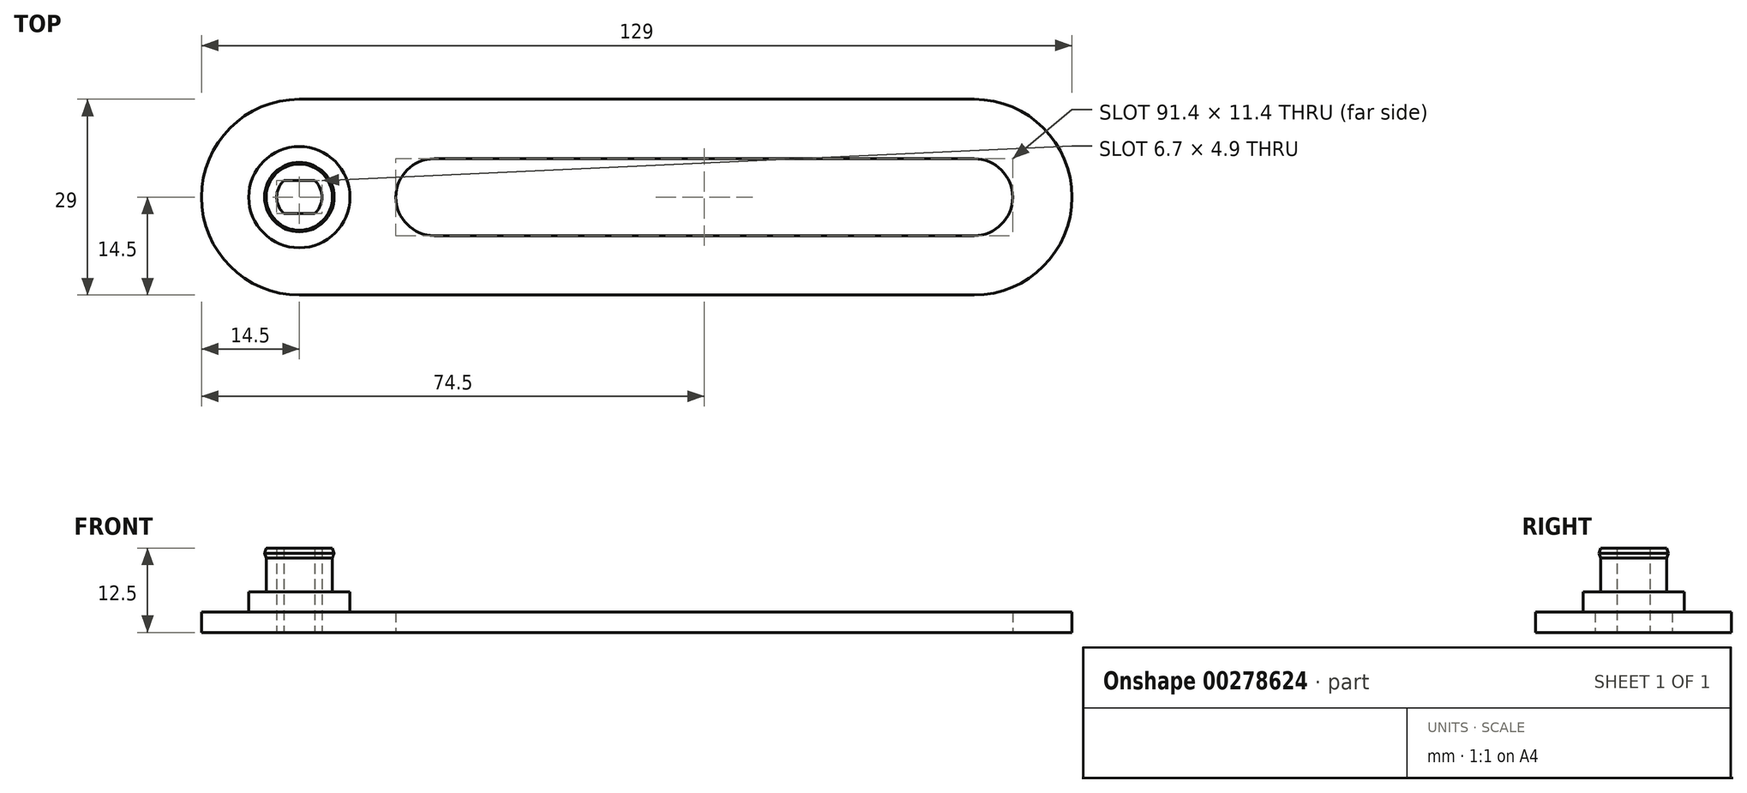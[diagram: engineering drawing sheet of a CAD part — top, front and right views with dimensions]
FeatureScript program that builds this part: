
annotation { "Feature Type Name" : "Feature", "Feature Type Description" : "" }
export const myFeature = defineFeature(function(context is Context, id is Id, definition is map)
    precondition{}
    {
        {
            assignVariable(context, id + "F0", {"name" : "e", "anyValue" : 3});
        }
        {
            assignVariable(context, id + "F1", {"name" : "h0", "anyValue" : 2});
        }
        {
            assignVariable(context, id + "F2", {"name" : "h1", "anyValue" : 3});
        }
        {
            assignVariable(context, id + "F3", {"name" : "h2", "anyValue" : 6.5});
        }
        {
            var Q0;
            Q0=qCreatedBy(makeId("Top.planeOp"),FACE);
            var sketch = newSketch(context, id + "F4", { "sketchPlane" : qUnion([Q0])});
            skCircle(sketch, "E0", {"center": v(0, 0) * mm, "radius": 5.5 * mm});
            skLineSegment(sketch, "E1.bottom", {"start": v(0, 14.5) * mm, "end": v(100, 14.5) * mm});
            skLineSegment(sketch, "E1.top", {"start": v(0, -14.5) * mm, "end": v(100, -14.5) * mm});
            skLineSegment(sketch, "E1.left", {"start": v(-14.5, 0) * mm, "end": v(-14.5, 0) * mm});
            skLineSegment(sketch, "E1.right", {"start": v(114.5, 0) * mm, "end": v(114.5, 0) * mm});
            skPoint(sketch, "E2", {"position": v(-14.5, 0) * mm});
            skPoint(sketch, "E3.visualSharp", {"position": v(114.5, 14.5) * mm});
            skArc(sketch, "E3.filletArc", {"start": v(114.5, 0) * mm, "mid": v(110.25, 10.25) * mm, "end": v(100, 14.5) * mm});
            skPoint(sketch, "E4.visualSharp", {"position": v(114.5, -14.5) * mm});
            skArc(sketch, "E4.filletArc", {"start": v(100, -14.5) * mm, "mid": v(110.25, -10.25) * mm, "end": v(114.5, 0) * mm});
            skPoint(sketch, "E5.visualSharp", {"position": v(-14.5, -14.5) * mm});
            skArc(sketch, "E5.filletArc", {"start": v(-14.5, 0) * mm, "mid": v(-10.25, -10.25) * mm, "end": v(0, -14.5) * mm});
            skPoint(sketch, "E6.visualSharp", {"position": v(-14.5, 14.5) * mm});
            skArc(sketch, "E6.filletArc", {"start": v(0, 14.5) * mm, "mid": v(-10.25, 10.25) * mm, "end": v(-14.5, 0) * mm});
            skPoint(sketch, "E7", {"position": v(20, 0) * mm});
            skLineSegment(sketch, "E8.bottom", {"start": v(20, 5.7) * mm, "end": v(100, 5.7) * mm});
            skLineSegment(sketch, "E8.top", {"start": v(20, -5.7) * mm, "end": v(100, -5.7) * mm});
            skLineSegment(sketch, "E8.left", {"start": v(20, 5.7) * mm, "end": v(20, -5.7) * mm, "construction": true});
            skLineSegment(sketch, "E8.right", {"start": v(100, 5.7) * mm, "end": v(100, -5.7) * mm, "construction": true});
            skArc(sketch, "E9", {"start": v(100, 5.7) * mm, "mid": v(105.7, 0) * mm, "end": v(100, -5.7) * mm});
            skArc(sketch, "E10", {"start": v(20, 5.7) * mm, "mid": v(14.3, 0) * mm, "end": v(20, -5.7) * mm});
            skCircle(sketch, "E11", {"center": v(0, 0) * mm, "radius": 7.5 * mm});
            skSolve(sketch);
        }
        {
            var Q0;
            Q0=makeQuery(id+"F4.imprint","IMPRINT",FACE,{"disambiguationData":[TD([[makeQuery(id+"F4.imprint","IMPRINT",EDGE,{"derivedFrom":sQuery(id+"F4.wireOp",EDGE,"E1.bottom")}),-1.0]])]});
            var Q1;
            Q1=makeQuery(id+"F4.imprint","IMPRINT",FACE,{"disambiguationData":[TD([[makeQuery(id+"F4.imprint","IMPRINT",EDGE,{"derivedFrom":sQuery(id+"F4.wireOp",EDGE,"E0")}),-1.0]])]});
            extrude(context, id + "F5", {"entities" : qUnion([Q0, Q1]), "depth" : (getVariable(context, 'e')) * mm});
        }
        {
            var Q0;
            Q0=makeQuery(id+"F4.imprint","IMPRINT",FACE,{"disambiguationData":[TD([[makeQuery(id+"F4.imprint","IMPRINT",EDGE,{"derivedFrom":sQuery(id+"F4.wireOp",EDGE,"E0")}),-1.0]])]});
            extrude(context, id + "F6", {"entities" : qUnion([Q0]), "operationType" : NewBodyOperationType.ADD, "depth" : (getVariable(context, 'e') + getVariable(context, 'h0')) * mm});
        }
        {
            var Q0;
            Q0=qCreatedBy(makeId("Top.planeOp"),FACE);
            var sketch = newSketch(context, id + "F7", { "sketchPlane" : qUnion([Q0])});
            skCircle(sketch, "E12", {"center": v(0, 0) * mm, "radius": 9.5 * mm});
            skCircle(sketch, "E13", {"center": v(0, 0) * mm, "radius": 7.5 * mm});
            skCircle(sketch, "E14", {"center": v(0, 0) * mm, "radius": 4.9 * mm});
            skArc(sketch, "E15", {"start": v(-2.28, 2.45) * mm, "mid": v(-3.35, 0) * mm, "end": v(-2.28, -2.45) * mm});
            skLineSegment(sketch, "E16.bottom", {"start": v(2.28, -2.45) * mm, "end": v(-2.28, -2.45) * mm});
            skLineSegment(sketch, "E16.top", {"start": v(2.28, 2.45) * mm, "end": v(-2.28, 2.45) * mm});
            skArc(sketch, "E17.trimOffspring", {"start": v(2.28, -2.45) * mm, "mid": v(3.35, 0) * mm, "end": v(2.28, 2.45) * mm});
            skPoint(sketch, "E18.orphan", {"position": v(3.35, -2.45) * mm});
            skPoint(sketch, "E19.orphan", {"position": v(-3.35, 2.45) * mm});
            skSolve(sketch);
        }
        {
            var Q0;
            Q0=qSketchRegion(id+"F7",true);
            var Q1;
            Q1=makeQuery(id+"F7.imprint","IMPRINT",FACE,{"disambiguationData":[TD([[makeQuery(id+"F7.imprint","IMPRINT",EDGE,{"derivedFrom":sQuery(id+"F7.wireOp",EDGE,"E13")}),1.0]])]});
            var Q2;
            Q2=makeQuery(id+"F7.imprint","IMPRINT",FACE,{"disambiguationData":[TD([[makeQuery(id+"F7.imprint","IMPRINT",EDGE,{"derivedFrom":sQuery(id+"F7.wireOp",EDGE,"E14")}),1.0]])]});
            extrude(context, id + "F8", {"entities" : qUnion([Q0, Q1, Q2]), "depth" : (getVariable(context, 'e')) * mm});
        }
        {
            var Q0;
            Q0=makeQuery(id+"F7.imprint","IMPRINT",FACE,{"disambiguationData":[TD([[makeQuery(id+"F7.imprint","IMPRINT",EDGE,{"derivedFrom":sQuery(id+"F7.wireOp",EDGE,"E13")}),1.0]])]});
            var Q1;
            Q1=makeQuery(id+"F7.imprint","IMPRINT",FACE,{"disambiguationData":[TD([[makeQuery(id+"F7.imprint","IMPRINT",EDGE,{"derivedFrom":sQuery(id+"F7.wireOp",EDGE,"E14")}),1.0]])]});
            extrude(context, id + "F9", {"entities" : qUnion([Q0, Q1]), "operationType" : NewBodyOperationType.ADD, "depth" : (getVariable(context, 'e') + getVariable(context, 'h1')) * mm});
        }
        {
            var Q0;
            Q0=makeQuery(id+"F7.imprint","IMPRINT",FACE,{"disambiguationData":[TD([[makeQuery(id+"F7.imprint","IMPRINT",EDGE,{"derivedFrom":sQuery(id+"F7.wireOp",EDGE,"E14")}),1.0]])]});
            extrude(context, id + "F10", {"entities" : qUnion([Q0]), "operationType" : NewBodyOperationType.ADD, "depth" : (getVariable(context, 'e') + getVariable(context, 'h1') + getVariable(context, 'h2')) * mm});
        }
        {
            var Q0;
            Q0=qCreatedBy(makeId("Front.planeOp"),FACE);
            var sketch = newSketch(context, id + "F11", { "sketchPlane" : qUnion([Q0])});
            skLineSegment(sketch, "E20", {"start": v(0, 0) * mm, "end": v(0, 17.26) * mm, "construction": true});
            skLineSegment(sketch, "E21", {"start": v(-4.9, 6) * mm, "end": v(-4.9, 12.5) * mm});
            skLineSegment(sketch, "E22", {"start": v(4.9, 12.5) * mm, "end": v(4.9, 6) * mm});
            skPoint(sketch, "E23", {"position": v(4.9, 12.5) * mm});
            skLineSegment(sketch, "E24.bottom", {"start": v(4.9, 12.5) * mm, "end": v(5.15, 12.5) * mm, "construction": true});
            skLineSegment(sketch, "E24.top", {"start": v(4.9, 11) * mm, "end": v(5.15, 11) * mm, "construction": true});
            skLineSegment(sketch, "E24.left", {"start": v(4.9, 12.5) * mm, "end": v(4.9, 11) * mm, "construction": true});
            skLineSegment(sketch, "E24.right", {"start": v(5.15, 12.5) * mm, "end": v(5.15, 11) * mm, "construction": true});
            skPoint(sketch, "E25", {"position": v(5.15, 11.75) * mm});
            skLineSegment(sketch, "E26", {"start": v(4.9, 12.5) * mm, "end": v(5.15, 11.75) * mm});
            skLineSegment(sketch, "E27", {"start": v(5.15, 11.75) * mm, "end": v(4.9, 11) * mm});
            skLineSegment(sketch, "E28", {"start": v(4.9, 11) * mm, "end": v(4.9, 12.5) * mm});
            skSolve(sketch);
        }
        {
            var Q0;
            Q0=qSketchRegion(id+"F11",true);
            var Q1;
            Q1=sQuery(id+"F11.wireOp",EDGE,"E20");
            revolve(context, id + "F12", {"operationType" : NewBodyOperationType.ADD, "entities" : qUnion([Q0]), "axis" : qUnion([Q1]), "revolveType" : RevolveType.FULL});
        }
    });
